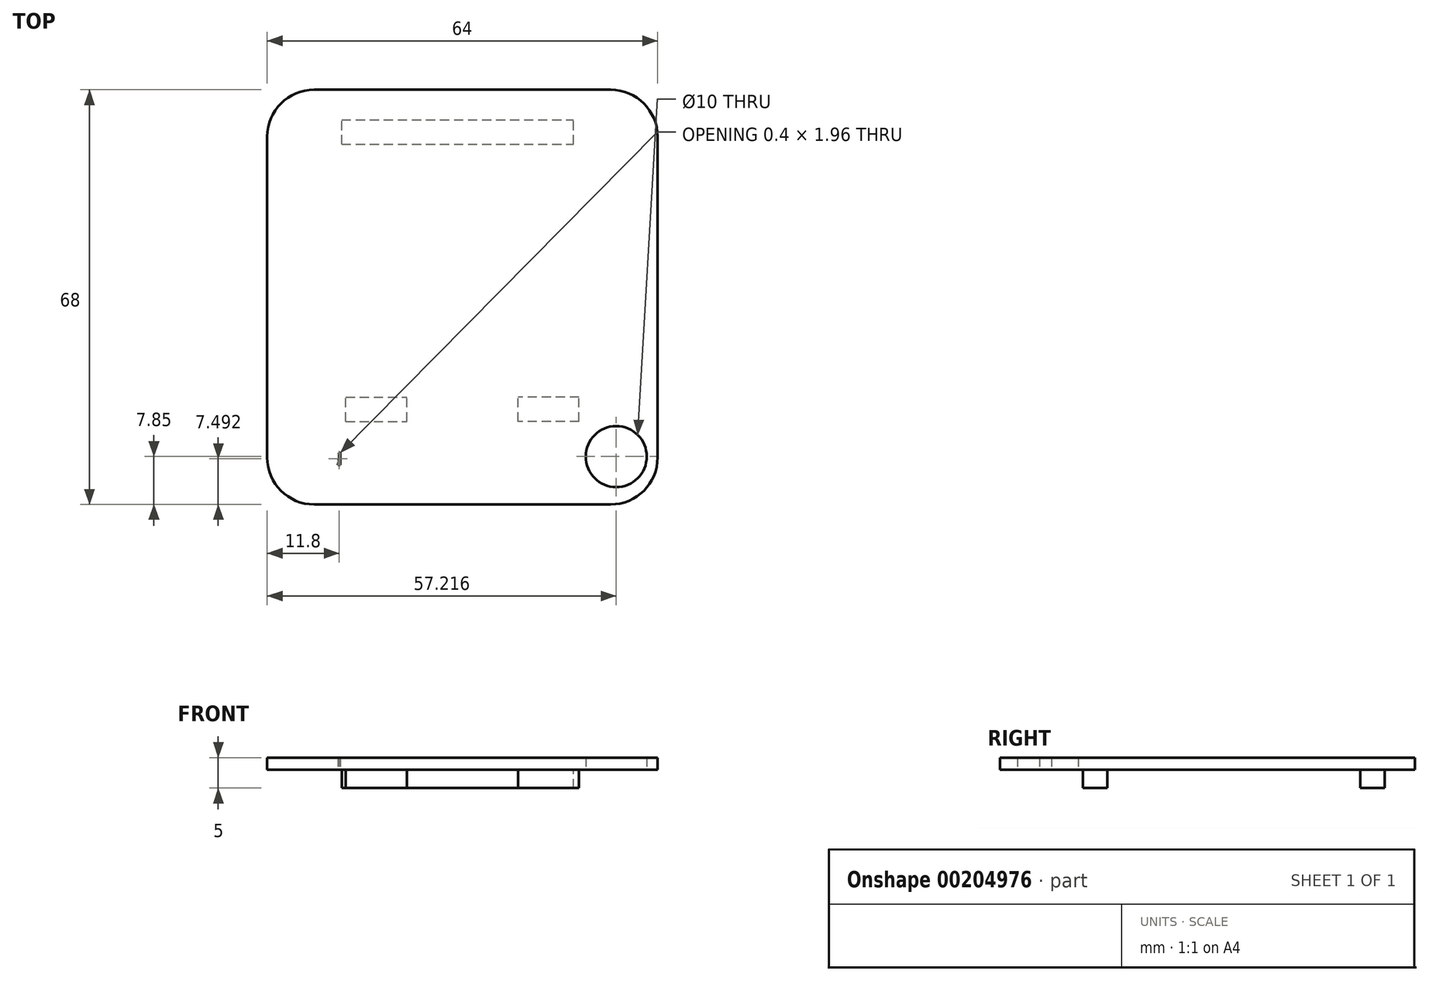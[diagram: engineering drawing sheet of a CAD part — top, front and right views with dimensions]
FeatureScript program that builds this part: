
annotation { "Feature Type Name" : "Feature", "Feature Type Description" : "" }
export const myFeature = defineFeature(function(context is Context, id is Id, definition is map)
    precondition{}
    {
        {
            var Q0;
            Q0=qCreatedBy(makeId("Top.planeOp"),FACE);
            var sketch = newSketch(context, id + "F0", { "sketchPlane" : qUnion([Q0])});
            skLineSegment(sketch, "E0.bottom", {"start": v(-24.3, 34) * mm, "end": v(24.3, 34) * mm});
            skLineSegment(sketch, "E0.top", {"start": v(-24.3, -34) * mm, "end": v(24.3, -34) * mm});
            skLineSegment(sketch, "E0.left", {"start": v(-32, 26.3) * mm, "end": v(-32, -26.3) * mm});
            skLineSegment(sketch, "E0.right", {"start": v(32, 26.3) * mm, "end": v(32, -26.3) * mm});
            skPoint(sketch, "E0.middle", {"position": v(0, 0) * mm});
            skPoint(sketch, "E1.visualSharp", {"position": v(32, 34) * mm});
            skArc(sketch, "E1.filletArc", {"start": v(32, 26.3) * mm, "mid": v(29.75, 31.75) * mm, "end": v(24.3, 34) * mm});
            skPoint(sketch, "E2.visualSharp", {"position": v(-32, 34) * mm});
            skArc(sketch, "E2.filletArc", {"start": v(-24.3, 34) * mm, "mid": v(-29.75, 31.75) * mm, "end": v(-32, 26.3) * mm});
            skPoint(sketch, "E3.visualSharp", {"position": v(-32, -34) * mm});
            skArc(sketch, "E3.filletArc", {"start": v(-32, -26.3) * mm, "mid": v(-29.75, -31.75) * mm, "end": v(-24.3, -34) * mm});
            skPoint(sketch, "E4.visualSharp", {"position": v(32, -34) * mm});
            skArc(sketch, "E4.filletArc", {"start": v(24.3, -34) * mm, "mid": v(29.75, -31.75) * mm, "end": v(32, -26.3) * mm});
            skLineSegment(sketch, "E5", {"start": v(0, -34) * mm, "end": v(0, -32) * mm});
            skPoint(sketch, "E5.endSnap0", {"position": v(0, -34) * mm});
            skCircle(sketch, "E6", {"center": v(-25.22, -26.15) * mm, "radius": 5 * mm});
            skCircle(sketch, "E7.MirrorC", {"center": v(25.22, -26.15) * mm, "radius": 5 * mm});
            skLineSegment(sketch, "E8.MirrorCS", {"start": v(30.68, -30.61) * mm, "end": v(28.93, -29.65) * mm});
            skLineSegment(sketch, "E9.bottom", {"start": v(-30.5, 21.3) * mm, "end": v(30.5, 21.3) * mm});
            skLineSegment(sketch, "E9.top", {"start": v(-30.5, -14.7) * mm, "end": v(30.5, -14.7) * mm});
            skLineSegment(sketch, "E9.left", {"start": v(-30.5, 21.3) * mm, "end": v(-30.5, -14.7) * mm});
            skLineSegment(sketch, "E9.right", {"start": v(30.5, 21.3) * mm, "end": v(30.5, -14.7) * mm});
            skLineSegment(sketch, "E10", {"start": v(-32, 15.13) * mm, "end": v(-30.5, 15.13) * mm});
            skLineSegment(sketch, "E11", {"start": v(30.5, 14.25) * mm, "end": v(32, 14.25) * mm});
            skLineSegment(sketch, "E12", {"start": v(-20.26, -25.53) * mm, "end": v(-20, -25.53) * mm});
            skLineSegment(sketch, "E13", {"start": v(-20, -25.53) * mm, "end": v(-20, -27.49) * mm});
            skLineSegment(sketch, "E14", {"start": v(-20, -27.49) * mm, "end": v(-20.4, -27.49) * mm});
            skLineSegment(sketch, "E15", {"start": v(20, -25.4) * mm, "end": v(20.27, -25.4) * mm});
            skLineSegment(sketch, "E16", {"start": v(20, -27.17) * mm, "end": v(20.32, -27.17) * mm});
            skSolve(sketch);
        }
        {
            var Q0;
            Q0=makeQuery(id+"F0.imprint","IMPRINT",FACE,{"disambiguationData":[TD([[makeQuery(id+"F0.imprint","IMPRINT",EDGE,{"derivedFrom":sQuery(id+"F0.wireOp",EDGE,"E0.bottom")}),-1.0]])]});
            var Q1;
            {var subQ5=sQuery(id+"F0.wireOp",EDGE,"fJw1VMtN-DNDU-9MxT-oK31-EzQkojQoViIx.bottom");Q1=makeQuery(id+"F0.imprint","IMPRINT",FACE,{"disambiguationData":[TD([[makeQuery(id+"F0.imprint","IMPRINT",EDGE,{"derivedFrom":subQ5}),-1.0]])]});}
            var Q2;
            {var subQ14=sQuery(id+"F0.wireOp",EDGE,"E3.filletArc");Q2=makeQuery(id+"F0.imprint","IMPRINT",FACE,{"disambiguationData":[TD([[makeQuery(id+"F0.imprint","IMPRINT",EDGE,{"derivedFrom":subQ14}),1.0]])]});}
            var Q3;
            {var subQ0=sQuery(id+"F0.wireOp",EDGE,"E5");Q3=makeQuery(id+"F0.imprint","IMPRINT",FACE,{"disambiguationData":[TD([[makeQuery(id+"F0.imprint","IMPRINT",EDGE,{"derivedFrom":subQ0}),-1.0]])]});}
            var Q4;
            {var subQ0=sQuery(id+"F0.wireOp",EDGE,"fJw1VMtN-DNDU-9MxT-oK31-EzQkojQoViIx.left");var subQ1=sQuery(id+"F0.wireOp",EDGE,"E9.bottom");var subQ2=makeQuery(id+"F0.imprint","INTERSECT",VERTEX,{"derivedFrom":[subQ1,subQ0]});Q4=makeQuery(id+"F0.imprint","IMPRINT",FACE,{"disambiguationData":[TD([[makeQuery(id+"F0.imprint","IMPRINT",EDGE,{"disambiguationData":[TD([[subQ2,-1.0]])],"derivedFrom":subQ1}),-1.0]])]});}
            var Q5;
            {var subQ0=sQuery(id+"F0.wireOp",EDGE,"E9.left");var subQ6=sQuery(id+"F0.wireOp",EDGE,"E9.bottom");var subQ7=makeQuery(id+"F0.imprint","INTERSECT",VERTEX,{"derivedFrom":[subQ6,subQ0]});Q5=makeQuery(id+"F0.imprint","IMPRINT",FACE,{"disambiguationData":[TD([[makeQuery(id+"F0.imprint","IMPRINT",EDGE,{"disambiguationData":[TD([[subQ7,-1.0]])],"derivedFrom":subQ6}),-1.0]])]});}
            var Q6;
            {var subQ0=sQuery(id+"F0.wireOp",EDGE,"E9.right");var subQ4=sQuery(id+"F0.wireOp",EDGE,"E9.bottom");var subQ5=makeQuery(id+"F0.imprint","INTERSECT",VERTEX,{"derivedFrom":[subQ4,subQ0]});Q6=makeQuery(id+"F0.imprint","IMPRINT",FACE,{"disambiguationData":[TD([[makeQuery(id+"F0.imprint","IMPRINT",EDGE,{"disambiguationData":[TD([[subQ5,1.0]])],"derivedFrom":subQ4}),-1.0]])]});}
            var Q7;
            {var subQ5=sQuery(id+"F0.wireOp",EDGE,"fJw1VMtN-DNDU-9MxT-oK31-EzQkojQoViIx.top");Q7=makeQuery(id+"F0.imprint","IMPRINT",FACE,{"disambiguationData":[TD([[makeQuery(id+"F0.imprint","IMPRINT",EDGE,{"derivedFrom":subQ5}),1.0]])]});}
            var Q8;
            {var subQ0=sQuery(id+"F0.wireOp",EDGE,"kw0yfpkd-Lx8Z-XIWm-CiKx-tGXYhEHlp0uT");Q8=makeQuery(id+"F0.imprint","IMPRINT",FACE,{"disambiguationData":[TD([[makeQuery(id+"F0.imprint","IMPRINT",EDGE,{"derivedFrom":subQ0}),-1.0]])]});}
            extrude(context, id + "F1", {"entities" : qUnion([Q0, Q1, Q2, Q3, Q4, Q5, Q6, Q7, Q8]), "depth" : 2 * mm});
        }
        {
            var Q0;
            Q0=makeQuery(id+"F0.imprint","IMPRINT",FACE,{"disambiguationData":[TD([[makeQuery(id+"F0.imprint","IMPRINT",EDGE,{"derivedFrom":sQuery(id+"F0.wireOp",EDGE,"E6")}),1.0]])]});
            var Q1;
            {var subQ0=sQuery(id+"F0.wireOp",EDGE,"E7.MirrorC");var subQ1=makeQuery(id+"F0.imprint","INTERSECT",VERTEX,{"derivedFrom":[subQ0,sQuery(id+"F0.wireOp",EDGE,"E8.MirrorCS")]});Q1=makeQuery(id+"F0.imprint","IMPRINT",FACE,{"disambiguationData":[TD([[makeQuery(id+"F0.imprint","IMPRINT",EDGE,{"disambiguationData":[TD([[subQ1,-1.0]])],"derivedFrom":subQ0}),-1.0]])]});}
            var Q2;
            {var subQ0=sQuery(id+"F0.wireOp",EDGE,"E7.MirrorC");var subQ1=makeQuery(id+"F0.imprint","IMPRINT",VERTEX,{"disambiguationData":[OD(0.0)],"derivedFrom":subQ0});Q2=makeQuery(id+"F0.imprint","IMPRINT",FACE,{"disambiguationData":[TD([[makeQuery(id+"F0.imprint","IMPRINT",EDGE,{"disambiguationData":[TD([[subQ1,-1.0]])],"derivedFrom":subQ0}),-1.0]])]});}
            extrude(context, id + "F2", {"entities" : qUnion([Q0, Q1, Q2]), "operationType" : NewBodyOperationType.ADD, "depth" : 2 * mm});
        }
        {
            var Q0;
            Q0=makeQuery(id+"F1.opExtrude","CAP_FACE",FACE,{"disambiguationData":[OSD([sQuery(id+"F0.wireOp",EDGE,"E0.bottom"),sQuery(id+"F0.wireOp",EDGE,"E0.top"),sQuery(id+"F0.wireOp",EDGE,"E0.left"),sQuery(id+"F0.wireOp",EDGE,"E0.right"),sQuery(id+"F0.wireOp",EDGE,"E1.filletArc"),sQuery(id+"F0.wireOp",EDGE,"E2.filletArc"),sQuery(id+"F0.wireOp",EDGE,"E3.filletArc"),sQuery(id+"F0.wireOp",EDGE,"E4.filletArc"),sQuery(id+"F0.wireOp",EDGE,"BVu8lub1-5okT-Fkh7-tBJV-ARj9UNPc45EQ.bottom"),sQuery(id+"F0.wireOp",EDGE,"BVu8lub1-5okT-Fkh7-tBJV-ARj9UNPc45EQ.top"),sQuery(id+"F0.wireOp",EDGE,"BVu8lub1-5okT-Fkh7-tBJV-ARj9UNPc45EQ.right"),sQuery(id+"F0.wireOp",EDGE,"Z9sNfQIX-WlfC-tEWu-jkLy-uOvkcjSQAIX6.bottom"),sQuery(id+"F0.wireOp",EDGE,"Z9sNfQIX-WlfC-tEWu-jkLy-uOvkcjSQAIX6.top"),sQuery(id+"F0.wireOp",EDGE,"Z9sNfQIX-WlfC-tEWu-jkLy-uOvkcjSQAIX6.right"),sQuery(id+"F0.wireOp",EDGE,"E6"),sQuery(id+"F0.wireOp",EDGE,"E7.MirrorC"),sQuery(id+"F0.wireOp",EDGE,"E12"),sQuery(id+"F0.wireOp",EDGE,"E14"),sQuery(id+"F0.wireOp",EDGE,"E15"),sQuery(id+"F0.wireOp",EDGE,"E16")])],"isStart":false});
            var sketch = newSketch(context, id + "F3", { "sketchPlane" : qUnion([Q0])});
            skLineSegment(sketch, "E17.bottom", {"start": v(-21.55, 31.23) * mm, "end": v(21.75, 31.23) * mm});
            skLineSegment(sketch, "E17.top", {"start": v(-21.55, -19.77) * mm, "end": v(21.75, -19.77) * mm});
            skLineSegment(sketch, "E17.left", {"start": v(-27.9, 24.88) * mm, "end": v(-27.9, -13.42) * mm});
            skLineSegment(sketch, "E17.right", {"start": v(28.1, 24.88) * mm, "end": v(28.1, -13.42) * mm});
            skPoint(sketch, "E18.visualSharp", {"position": v(-27.9, 31.23) * mm});
            skArc(sketch, "E18.filletArc", {"start": v(-21.55, 31.23) * mm, "mid": v(-26.04, 29.37) * mm, "end": v(-27.9, 24.88) * mm});
            skPoint(sketch, "E19.visualSharp", {"position": v(28.1, 31.23) * mm});
            skArc(sketch, "E19.filletArc", {"start": v(28.1, 24.88) * mm, "mid": v(26.24, 29.37) * mm, "end": v(21.75, 31.23) * mm});
            skPoint(sketch, "E20.visualSharp", {"position": v(28.1, -19.77) * mm});
            skArc(sketch, "E20.filletArc", {"start": v(21.75, -19.77) * mm, "mid": v(26.24, -17.91) * mm, "end": v(28.1, -13.42) * mm});
            skPoint(sketch, "E21.visualSharp", {"position": v(-27.9, -19.77) * mm});
            skArc(sketch, "E21.filletArc", {"start": v(-27.9, -13.42) * mm, "mid": v(-26.04, -17.91) * mm, "end": v(-21.55, -19.77) * mm});
            skLineSegment(sketch, "E22", {"start": v(8.8, -19.77) * mm, "end": v(8.8, -22.07) * mm});
            skLineSegment(sketch, "E23.MirrorCS", {"start": v(-8.8, -19.77) * mm, "end": v(-8.8, -22.07) * mm});
            skSolve(sketch);
        }
        {
            var Q0;
            Q0=makeQuery(id+"F0.imprint","IMPRINT",FACE,{"disambiguationData":[TD([[makeQuery(id+"F0.imprint","IMPRINT",EDGE,{"derivedFrom":sQuery(id+"F0.wireOp",EDGE,"E0.bottom")}),-1.0]])]});
            var sketch = newSketch(context, id + "F4", { "sketchPlane" : qUnion([Q0])});
            skLineSegment(sketch, "E24.bottom", {"start": v(-19.78, 25.06) * mm, "end": v(18.22, 25.06) * mm});
            skLineSegment(sketch, "E24.top", {"start": v(-19.78, 29.06) * mm, "end": v(18.22, 29.06) * mm});
            skLineSegment(sketch, "E24.left", {"start": v(-19.78, 25.06) * mm, "end": v(-19.78, 29.06) * mm});
            skLineSegment(sketch, "E24.right", {"start": v(18.22, 25.06) * mm, "end": v(18.22, 29.06) * mm});
            skLineSegment(sketch, "E25.bottom", {"start": v(-19.1, -20.38) * mm, "end": v(-9.1, -20.38) * mm});
            skLineSegment(sketch, "E25.top", {"start": v(-19.1, -16.38) * mm, "end": v(-9.1, -16.38) * mm});
            skLineSegment(sketch, "E25.left", {"start": v(-19.1, -20.38) * mm, "end": v(-19.1, -16.38) * mm});
            skLineSegment(sketch, "E25.right", {"start": v(-9.1, -20.38) * mm, "end": v(-9.1, -16.38) * mm});
            skLineSegment(sketch, "E26.MirrorCS", {"start": v(19.1, -20.38) * mm, "end": v(9.1, -20.38) * mm});
            skLineSegment(sketch, "E27.MirrorCS", {"start": v(19.1, -20.38) * mm, "end": v(19.1, -16.38) * mm});
            skLineSegment(sketch, "E28.MirrorCS", {"start": v(9.1, -20.38) * mm, "end": v(9.1, -16.38) * mm});
            skLineSegment(sketch, "E29.MirrorCS", {"start": v(19.1, -16.38) * mm, "end": v(9.1, -16.38) * mm});
            skLineSegment(sketch, "E30", {"start": v(20.95, 29.83) * mm, "end": v(24.56, 30.15) * mm});
            skLineSegment(sketch, "E31", {"start": v(-22.36, 29.83) * mm, "end": v(-24.8, 30.9) * mm});
            skSolve(sketch);
        }
        {
            var Q0;
            Q0=makeQuery(id+"F4.imprint","IMPRINT",FACE,{"disambiguationData":[TD([[makeQuery(id+"F4.imprint","IMPRINT",EDGE,{"derivedFrom":sQuery(id+"F4.wireOp",EDGE,"E24.bottom")}),1.0]])]});
            var Q1;
            Q1=makeQuery(id+"F4.imprint","IMPRINT",FACE,{"disambiguationData":[TD([[makeQuery(id+"F4.imprint","IMPRINT",EDGE,{"derivedFrom":sQuery(id+"F4.wireOp",EDGE,"E26.MirrorCS")}),-1.0]])]});
            var Q2;
            Q2=makeQuery(id+"F4.imprint","IMPRINT",FACE,{"disambiguationData":[TD([[makeQuery(id+"F4.imprint","IMPRINT",EDGE,{"derivedFrom":sQuery(id+"F4.wireOp",EDGE,"E25.bottom")}),1.0]])]});
            extrude(context, id + "F5", {"entities" : qUnion([Q0, Q1, Q2]), "operationType" : NewBodyOperationType.ADD, "oppositeDirection" : true, "depth" : 3 * mm});
        }
    });
